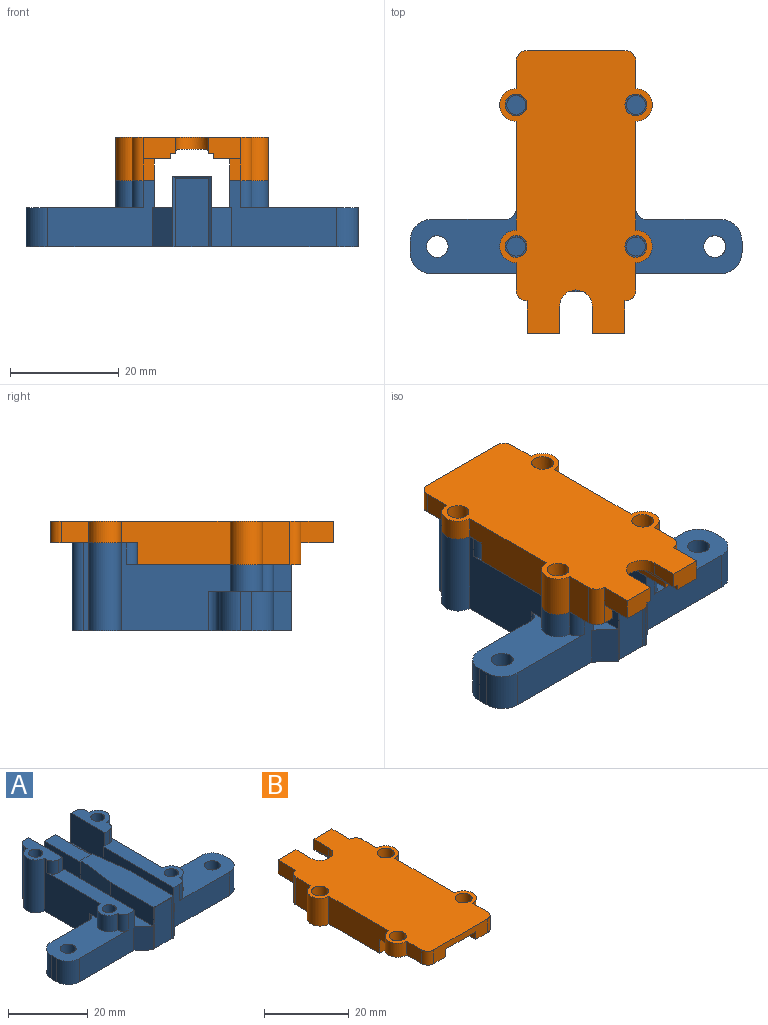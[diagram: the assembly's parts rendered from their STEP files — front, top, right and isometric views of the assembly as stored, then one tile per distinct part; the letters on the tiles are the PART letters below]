
ASSEMBLY  parts=2 mates=1
PART A: 69 faces, bbox 61x40.3x16.2 mm
  f0: plane 15.33x5.8mm, normal (-1,0,0), area 88.9mm2, adj f9,f14,f16,f32
  f1: plane 15.33x5.8mm, normal (1,0,0), area 88.9mm2, adj f5,f14,f17,f33
  f2: plane 19.6x12.2mm, normal (0,-1,0), area 149.3mm2, adj f3,f5,f15,f25,f51,f52,f59,f67
  f3: plane 21.5x12mm, normal (0,0,1), area 163.1mm2, adj f2,f7,f22,f23,f24,f25,f26,f54
  f4: plane 21.5x12mm, normal (0,0,1), area 163.1mm2, adj f6,f10,f18,f19,f20,f21,f27,f53
  f5: plane 40.33x5.5mm, normal (0,0,1), area 167.7mm2, adj f1,f2,f11,f29,f33,f38,f50,f51
  f6: plane 20x16.2mm, normal (-1,0,0), area 219.2mm2, adj f4,f15,f37,f42,f49,f53,f62,f64
  f7: plane 20x16.2mm, normal (1,0,0), area 219.2mm2, adj f3,f15,f40,f41,f52,f54,f61,f63
  f8: plane 13x5.2mm, normal (-1,0,0), area 67.6mm2, adj f9,f28,f29,f32
  f9: plane 40.33x5.5mm, normal (0,0,1), area 167.7mm2, adj f0,f8,f18,f29,f32,f35,f47,f48
  f10: plane 13.5x7.2mm, normal (0,1,0), area 97.2mm2, adj f4,f15,f21,f64
  f11: plane 13x5.2mm, normal (1,0,0), area 67.6mm2, adj f5,f28,f29,f33
  f12: plane 12.5x6mm, normal (0,-1,0), area 75mm2, adj f13,f15,f16,f17
  f13: plane 7x0.5mm, normal (0,-0.83,-0.55), area 3.9mm2, adj f12,f14,f16,f17
  f14: plane 27.33x7mm, normal (0,0,1), area 173.3mm2, adj f0,f1,f13,f32,f33,f34
  f15: plane 61x40.33mm, normal (0,0,-1), area 1227mm2, adj f2,f6,f7,f10,f12,f16,f17,f18
  f16: plane 13x0.5mm, normal (0.55,-0.83,0), area 7.7mm2, adj f0,f12,f13,f15,f68
  f17: plane 13x0.5mm, normal (-0.55,-0.83,0), area 7.6mm2, adj f1,f12,f13,f15,f67
  f18: plane 19.6x12.2mm, normal (0,-1,0), area 149.3mm2, adj f4,f9,f15,f19,f48,f49,f60,f68
  f19: cylinder r=4mm len=7.2mm, axis (0,0,-1), area 45.2mm2, adj f4,f15,f18,f20
  f20: plane 7.2x2mm, normal (-1,0,0), area 14.4mm2, adj f4,f15,f19,f21
  f21: cylinder r=4mm len=7.2mm, axis (0,0,-1), area 45.2mm2, adj f4,f10,f15,f20
  f22: plane 13.5x7.2mm, normal (0,1,0), area 97.2mm2, adj f3,f15,f23,f63
  f23: cylinder r=4mm len=7.2mm, axis (0,0,-1), area 45.2mm2, adj f3,f15,f22,f24
  f24: plane 7.2x2mm, normal (1,0,0), area 14.4mm2, adj f3,f15,f23,f25
  f25: cylinder r=4mm len=7.2mm, axis (0,0,-1), area 45.2mm2, adj f2,f3,f15,f24
  f26: cylinder r=2mm len=7.2mm, axis (0,0,-1), area 90.5mm2, adj f3,f15
  f27: cylinder r=2mm len=7.2mm, axis (0,0,-1), area 90.5mm2, adj f4,f15
  f28: plane 13x4mm, normal (0,0,1), area 52mm2, adj f8,f11,f29,f34
  f29: plane 18x16.2mm, normal (0,1,0), area 177.4mm2, adj f5,f8,f9,f11,f15,f28,f35,f37
  f30: plane 16.2x1mm, normal (1,0,0), area 16.2mm2, adj f15,f40,f41,f66
  f31: plane 16.2x1mm, normal (-1,0,0), area 16.2mm2, adj f15,f37,f42,f65
  f32: plane 12x5.8mm, normal (-0.99,0.12,0), area 70.1mm2, adj f0,f8,f9,f14,f34
  f33: plane 12x5.8mm, normal (0.99,0.12,0), area 70.1mm2, adj f1,f5,f11,f14,f34
  f34: plane 4x0.6mm, normal (0,1,0), area 2.4mm2, adj f14,f28,f32,f33
  f35: plane 12x9mm, normal (1,0,0), area 108mm2, adj f9,f29,f36,f37,f47
  f36: plane 4x1.5mm, normal (0,-1,0), area 6mm2, adj f35,f37,f49,f62
  f37: plane 12x6.5mm, normal (0,0,1), area 44.8mm2, adj f6,f29,f31,f35,f36,f42,f43,f62
  f38: plane 12x9mm, normal (-1,0,0), area 108mm2, adj f5,f29,f39,f40,f50
  f39: plane 4x1.5mm, normal (0,-1,0), area 6mm2, adj f38,f40,f52,f61
  f40: plane 12x6.5mm, normal (0,0,1), area 44.8mm2, adj f7,f29,f30,f38,f39,f41,f45,f61
  f41: cylinder r=3mm len=16.2mm, axis (0,0,1), area 152.7mm2, adj f7,f15,f30,f40
  f42: cylinder r=3mm len=16.2mm, axis (0,0,1), area 152.7mm2, adj f6,f15,f31,f37
  f43: cylinder r=1.75mm len=12mm, axis (0,0,1), area 131.9mm2, adj f37,f44
  f44: plane 3.5x3.5mm, normal (0,0,1), area 9.6mm2, adj f43
  f45: cylinder r=1.75mm len=12mm, axis (0,0,1), area 131.9mm2, adj f40,f46
  f46: plane 3.5x3.5mm, normal (0,0,1), area 9.6mm2, adj f45
  f47: plane 5x0.6mm, normal (0,1,0), area 3mm2, adj f9,f35,f48,f49
  f48: plane 25x5mm, normal (1,0,0), area 125mm2, adj f9,f18,f47,f49
  f49: plane 27x7.1mm, normal (0,0,1), area 107mm2, adj f6,f18,f36,f47,f48,f53,f55,f60
  f50: plane 5x0.6mm, normal (0,1,0), area 3mm2, adj f5,f38,f51,f52
  f51: plane 25x5mm, normal (-1,0,0), area 125mm2, adj f2,f5,f50,f52
  f52: plane 27x7.1mm, normal (0,0,1), area 107mm2, adj f2,f7,f39,f50,f51,f54,f57,f59
  f53: cylinder r=3mm len=6mm, axis (0,0,1), area 47.1mm2, adj f4,f6,f49,f60
  f54: cylinder r=3mm len=6mm, axis (0,0,1), area 47.1mm2, adj f3,f7,f52,f59
  f55: cylinder r=1.75mm len=10mm, axis (0,0,1), area 110mm2, adj f49,f56
  f56: plane 3.5x3.5mm, normal (0,0,1), area 9.6mm2, adj f55
  f57: cylinder r=1.75mm len=10mm, axis (0,0,1), area 110mm2, adj f52,f58
  f58: plane 3.5x3.5mm, normal (0,0,1), area 9.6mm2, adj f57
  f59: cylinder r=2mm len=5mm, axis (0,0,-1), area 15.7mm2, adj f2,f3,f52,f54
  f60: cylinder r=2mm len=5mm, axis (0,0,-1), area 15.7mm2, adj f4,f18,f49,f53
  f61: cylinder r=2mm len=4mm, axis (0,0,1), area 12.6mm2, adj f7,f39,f40,f52
  f62: cylinder r=2mm len=4mm, axis (0,0,1), area 12.6mm2, adj f6,f36,f37,f49
  f63: cylinder r=2mm len=7.2mm, axis (0,0,-1), area 22.6mm2, adj f3,f7,f15,f22
  f64: cylinder r=2mm len=7.2mm, axis (0,0,1), area 22.6mm2, adj f4,f6,f10,f15
  f65: cylinder r=2mm len=16.2mm, axis (0,0,-1), area 50.9mm2, adj f15,f29,f31,f37
  f66: cylinder r=2mm len=16.2mm, axis (0,0,1), area 50.9mm2, adj f15,f29,f30,f40
  f67: plane 7.2x3.73mm, normal (0.67,-0.75,0), area 36mm2, adj f2,f5,f15,f17
  f68: plane 7.2x3.73mm, normal (-0.67,-0.75,0), area 36mm2, adj f9,f15,f16,f18
PART B: 47 faces, bbox 28x52x8 mm
  f0: plane 52x28mm, normal (0,0,1), area 1078.7mm2, adj f1,f7,f8,f9,f10,f11,f12,f13
  f1: plane 6x4mm, normal (0,1,0), area 23mm2, adj f0,f2,f18,f37,f41,f44
  f2: plane 10x8mm, normal (0,-0.1,-1), area 36mm2, adj f1,f3,f39,f40,f41,f44,f45,f46
  f3: plane 25x9mm, normal (0,0,-1), area 207.2mm2, adj f2,f22,f40,f41,f42,f43
  f4: plane 52x10mm, normal (0,0,-1), area 209.1mm2, adj f5,f7,f10,f12,f13,f15,f21,f22
  f5: plane 4x2.1mm, normal (0,1,0), area 8.4mm2, adj f4,f23,f25,f33
  f6: plane 4x2.1mm, normal (0,1,0), area 8.4mm2, adj f18,f26,f28,f36
  f7: cylinder r=3mm len=6mm, axis (0,0,1), area 37.7mm2, adj f0,f4,f12,f13
  f8: cylinder r=3mm len=6mm, axis (0,0,1), area 37.7mm2, adj f0,f11,f14,f18
  f9: cylinder r=2mm len=4mm, axis (0,0,1), area 50.3mm2, adj f0,f18
  f10: cylinder r=2mm len=4mm, axis (0,0,1), area 50.3mm2, adj f0,f4
  f11: plane 5x4mm, normal (1,0,0), area 20mm2, adj f0,f8,f18,f35
  f12: plane 5x4mm, normal (-1,0,0), area 20mm2, adj f0,f4,f7,f34
  f13: plane 20x8mm, normal (-1,0,0), area 148mm2, adj f0,f4,f7,f24,f25,f30
  f14: plane 20x8mm, normal (1,0,0), area 148mm2, adj f0,f8,f18,f27,f28,f29
  f15: plane 18x4mm, normal (0,-1,0), area 50mm2, adj f0,f4,f18,f19,f20,f21,f34,f35
  f16: plane 8x5mm, normal (-1,0,0), area 40mm2, adj f0,f25,f30,f33
  f17: plane 8x5mm, normal (1,0,0), area 40mm2, adj f0,f28,f29,f36
  f18: plane 52x10mm, normal (0,0,-1), area 209.1mm2, adj f1,f6,f8,f9,f11,f14,f15,f19
  f19: plane 17x2.2mm, normal (-1,0,0), area 37.4mm2, adj f15,f18,f20,f22
  f20: plane 17x10mm, normal (0,0,-1), area 170mm2, adj f15,f19,f21,f22
  f21: plane 17x2.2mm, normal (1,0,0), area 37.4mm2, adj f4,f15,f20,f22
  f22: plane 10x2.2mm, normal (0,-1,0), area 4mm2, adj f3,f4,f18,f19,f20,f21,f42,f43
  f23: plane 30x4mm, normal (1,0,0), area 120mm2, adj f4,f5,f24,f25
  f24: plane 4.1x4mm, normal (0,-1,0), area 16.4mm2, adj f4,f13,f23,f25
  f25: plane 30x7.1mm, normal (0,0,-1), area 123.7mm2, adj f5,f13,f16,f23,f24,f30,f32,f33
  f26: plane 30x4mm, normal (-1,0,0), area 120mm2, adj f6,f18,f27,f28
  f27: plane 4.1x4mm, normal (0,-1,0), area 16.4mm2, adj f14,f18,f26,f28
  f28: plane 30x7.1mm, normal (0,0,-1), area 123.7mm2, adj f6,f14,f17,f26,f27,f29,f31,f36
  f29: cylinder r=3mm len=8mm, axis (0,0,1), area 75.4mm2, adj f0,f14,f17,f28
  f30: cylinder r=3mm len=8mm, axis (0,0,1), area 75.4mm2, adj f0,f13,f16,f25
  f31: cylinder r=2mm len=8mm, axis (0,0,1), area 100.5mm2, adj f0,f28
  f32: cylinder r=2mm len=8mm, axis (0,0,1), area 100.5mm2, adj f0,f25
  f33: cylinder r=2mm len=8mm, axis (0,0,-1), area 25.1mm2, adj f0,f5,f16,f25,f38
  f34: cylinder r=2mm len=4mm, axis (0,0,1), area 12.6mm2, adj f0,f4,f12,f15
  f35: cylinder r=2mm len=4mm, axis (0,0,-1), area 12.6mm2, adj f0,f11,f15,f18
  f36: cylinder r=2mm len=8mm, axis (0,0,1), area 25.1mm2, adj f0,f6,f17,f28,f37
  f37: plane 6x4mm, normal (1,0,0), area 24mm2, adj f0,f1,f18,f36
  f38: plane 6x4mm, normal (-1,0,0), area 24mm2, adj f0,f4,f33,f39
  f39: plane 6x4mm, normal (0,1,0), area 23mm2, adj f0,f2,f4,f38,f40,f45
  f40: plane 20.68x2mm, normal (1,0,0), area 36.4mm2, adj f2,f3,f4,f39,f43
  f41: plane 20.68x2mm, normal (-1,0,0), area 36.4mm2, adj f1,f2,f3,f18,f42
  f42: plane 14.32x2mm, normal (-1,-0.03,0), area 28.7mm2, adj f3,f18,f22,f41
  f43: plane 14.32x2mm, normal (1,-0.03,0), area 28.7mm2, adj f3,f4,f22,f40
  f44: plane 5x3mm, normal (-1,0,0), area 13.7mm2, adj f0,f1,f2,f46
  f45: plane 5x3mm, normal (1,0,0), area 13.7mm2, adj f0,f2,f39,f46
  f46: cylinder r=3mm len=6mm, axis (0,0,1), area 21.8mm2, adj f0,f2,f44,f45
PLACE A t=(-8.8,5.48,7.64)mm
PLACE B rot(axis=(0,0,-1),180deg) t=(5.7,49.48,23.84)mm
MATE fastened A.f42 <-> B.f8  axis (0,0,1) through (-16.3,39.48,23.84)mm
